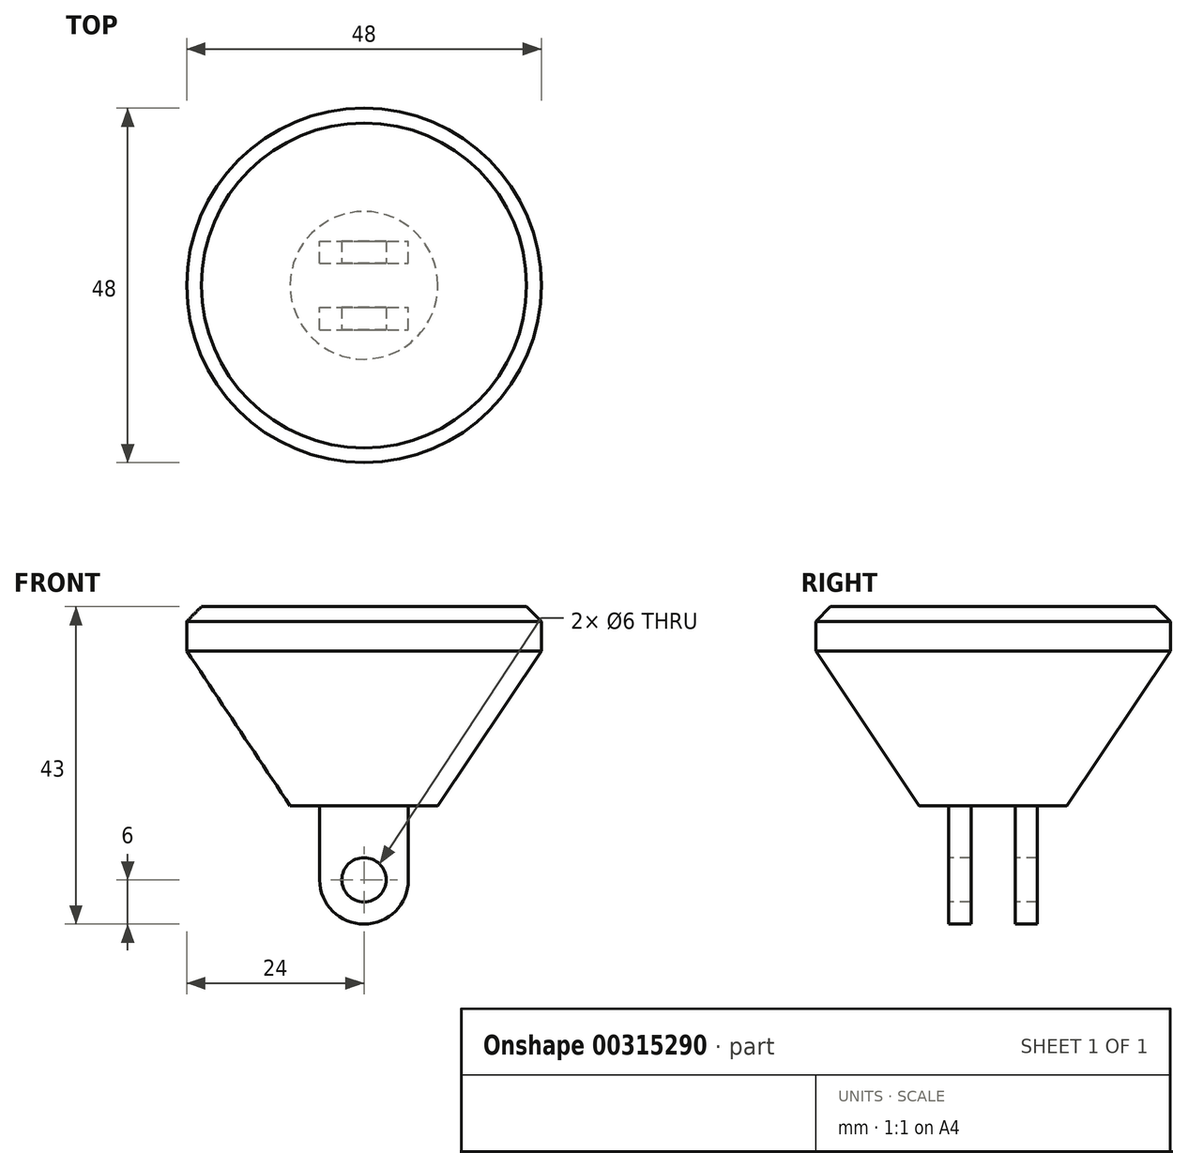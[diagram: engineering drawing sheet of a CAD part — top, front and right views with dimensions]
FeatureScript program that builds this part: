
annotation { "Feature Type Name" : "Feature", "Feature Type Description" : "" }
export const myFeature = defineFeature(function(context is Context, id is Id, definition is map)
    precondition{}
    {
        {
            var Q0;
            Q0=qCreatedBy(makeId("Front.planeOp"),FACE);
            var sketch = newSketch(context, id + "F0", { "sketchPlane" : qUnion([Q0])});
            skLineSegment(sketch, "E0", {"start": v(0, 0) * mm, "end": v(0, 27) * mm});
            skLineSegment(sketch, "E1", {"start": v(0, 27) * mm, "end": v(-24, 27) * mm});
            skLineSegment(sketch, "E2", {"start": v(-24, 27) * mm, "end": v(-24, 21) * mm});
            skLineSegment(sketch, "E3", {"start": v(-24, 21) * mm, "end": v(-10, 0) * mm});
            skLineSegment(sketch, "E4", {"start": v(-10, 0) * mm, "end": v(0, 0) * mm});
            skLineSegment(sketch, "E5", {"start": v(-6, 0) * mm, "end": v(6, 0) * mm});
            skPoint(sketch, "E5.endSnap0", {"position": v(-5, 0) * mm});
            skLineSegment(sketch, "E6", {"start": v(6, 0) * mm, "end": v(6, -10) * mm});
            skLineSegment(sketch, "E7", {"start": v(-6, 0) * mm, "end": v(-6, -10) * mm});
            skArc(sketch, "E8", {"start": v(-6, -10) * mm, "mid": v(0, -16) * mm, "end": v(6, -10) * mm});
            skSolve(sketch);
        }
        {
            var Q0;
            {var subQ0=sQuery(id+"F0.wireOp",EDGE,"E0");Q0=makeQuery(id+"F0.imprint","IMPRINT",FACE,{"disambiguationData":[TD([[makeQuery(id+"F0.imprint","IMPRINT",EDGE,{"derivedFrom":subQ0}),1.0]])]});}
            var Q1;
            Q1=sQuery(id+"F0.wireOp",EDGE,"E0");
            revolve(context, id + "F1", {"entities" : qUnion([Q0]), "axis" : qUnion([Q1]), "revolveType" : RevolveType.FULL});
        }
        {
            var Q0;
            {var subQ1=sQuery(id+"F0.wireOp",EDGE,"E6");Q0=makeQuery(id+"F0.imprint","IMPRINT",FACE,{"disambiguationData":[TD([[makeQuery(id+"F0.imprint","IMPRINT",EDGE,{"derivedFrom":subQ1}),-1.0]])]});}
            extrude(context, id + "F2", {"entities" : qUnion([Q0]), "operationType" : NewBodyOperationType.ADD, "endBound" : BoundingType.SYMMETRIC, "depth" : 12 * mm});
        }
        {
            var Q0;
            {var subQ1=sQuery(id+"F0.wireOp",EDGE,"E6");Q0=makeQuery(id+"F0.imprint","IMPRINT",FACE,{"disambiguationData":[TD([[makeQuery(id+"F0.imprint","IMPRINT",EDGE,{"derivedFrom":subQ1}),-1.0]])]});}
            extrude(context, id + "F3", {"entities" : qUnion([Q0]), "operationType" : NewBodyOperationType.REMOVE, "endBound" : BoundingType.SYMMETRIC, "oppositeDirection" : true, "depth" : 6 * mm});
        }
        {
            var Q0;
            Q0=makeQuery(id+"F1.opRevolve","SWEPT_EDGE",EDGE,{"disambiguationData":[OSD([sQuery(id+"F0.wireOp",EDGE,"E1"),sQuery(id+"F0.wireOp",EDGE,"E2")])]});
            chamfer(context, id + "F4", {"entities" : qUnion([Q0]), "width" : 2 * mm, "tangentPropagation" : true});
        }
        {
            var Q0;
            Q0=makeQuery(id+"F2.opExtrude","CAP_FACE",FACE,{"disambiguationData":[OSD([sQuery(id+"F0.wireOp",EDGE,"E5"),sQuery(id+"F0.wireOp",EDGE,"E6"),sQuery(id+"F0.wireOp",EDGE,"E7"),sQuery(id+"F0.wireOp",EDGE,"E8")])],"isStart":false});
            var sketch = newSketch(context, id + "F5", { "sketchPlane" : qUnion([Q0])});
            skArc(sketch, "E9.0", {"start": v(-6, -10) * mm, "mid": v(0, -16) * mm, "end": v(6, -10) * mm, "construction": true});
            skSolve(sketch);
        }
        {
            var Q0;
            Q0=sQuery(id+"F5.wireOp",VERTEX,"E9.0.center");
            var Q1;
            Q1=makeQuery(id+"F1.opRevolve","SWEPT_BODY",BODY,{"disambiguationData":[OSD([sQuery(id+"F0.wireOp",EDGE,"E0"),sQuery(id+"F0.wireOp",EDGE,"E1"),sQuery(id+"F0.wireOp",EDGE,"E2"),sQuery(id+"F0.wireOp",EDGE,"E3"),sQuery(id+"F0.wireOp",EDGE,"E4"),sQuery(id+"F0.wireOp",EDGE,"E5")])]});
            hole(context, id + "F6", {"style" : HoleStyle.SIMPLE, "endStyle" : HoleEndStyle.THROUGH, "holeDiameter" : 6 * mm, "tappedDepth" : 12 * mm, "tapClearance" : 3, "locations" : qUnion([Q0]), "scope" : qUnion([Q1])});
        }
    });
